# Revit family: P-34V（M）I型
name_source: partatom
category: 一般モデル
revit_build: Autodesk Revit 2015 (Build: 20140606_1530(x64)
units: mm (PartAtom-declared; Revit-internal decimal feet)

## types (8) — shared parameters
N_仕様① = ●手すり本体　φ34　表面材：半硬質樹脂（抗菌剤入り）+軟質樹脂二層成形　※ウッドカラー（M)は超微粒子木粉配合　芯材：ステンレス鋼管φ27.2x1.0t　●ブラケット・ブラケットカバー　特殊ABS樹脂
N_品名 = バリアフリー補助手すり　ソフトハンド
N_回転角度 = 0.00°
N_手すり径 = 34
N_製造元 = ナカ工業株式会社

## per-type parameters (varying)
| type | N_L1 | N_マテリアル | N_形式① | N_形式② |
| P-34V（I-40) | 400  [stored 1.31234 ft] | 笠木No.00ホワイト | P-34V | I-40 |
| P-34V（I-50) | 500 | 笠木No.00ホワイト | P-34V | I-50 |
| P-34V（I-60) | 600 | 笠木No.00ホワイト | P-34V | I-60 |
| P-34V（I-80) | 800 | 笠木No.00ホワイト | P-34V | I-80 |
| P-34M（I-40) | 400  [stored 1.31234 ft] | 笠木No.73バーチ | P-34M | I-40 |
| P-34M（I-50) | 500 | 笠木No.73バーチ | P-34M | I-50 |
| P-34M（I-60) | 600 | 笠木No.73バーチ | P-34M | I-60 |
| P-34M（I-80) | 800 | 笠木No.73バーチ | P-34M | I-80 |

note: [stored X ft] marks values corroborated as IEEE doubles in the binary element streams (Revit-internal decimal feet)
